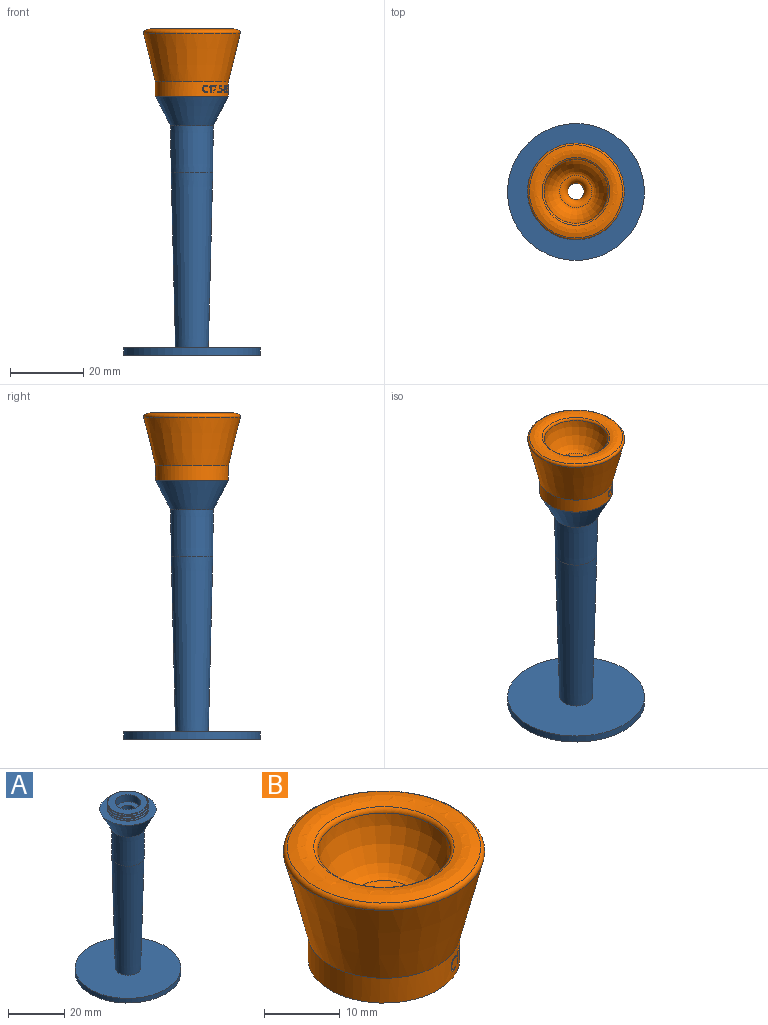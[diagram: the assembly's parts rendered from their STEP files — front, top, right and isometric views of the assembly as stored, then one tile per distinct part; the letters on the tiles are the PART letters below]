
ASSEMBLY  parts=2 mates=1
PART A: 17 faces, bbox 37.8x37.8x74.6 mm
  f0: plane 20.26x20.26mm, normal (0,0,1), area 156.7mm2, adj f4,f12,f13,f14,f15,f16
  f1: plane 37.5x37.5mm, normal (0,0,1), area 1040.8mm2, adj f2,f5
  f2: cone r=4.5mm half-angle=1.4deg, axis (0,0,1), area 1542.8mm2, adj f1,f3
  f3: cone r=5.7mm half-angle=0.6deg, axis (0,0,1), area 463.4mm2, adj f2,f4
  f4: cone r=5.84mm half-angle=27.5deg, axis (0,0,1), area 448.7mm2, adj f0,f3
  f5: cylinder r=18.75mm len=37.5mm, axis (0,0,-1), area 235.6mm2, adj f1,f6
  f6: plane 37.5x37.5mm, normal (0,0,-1), area 1060.3mm2, adj f5,f7
  f7: cylinder r=3.75mm len=7.5mm, axis (0,0,-1), area 47.1mm2, adj f6,f8
  f8: cone r=2.25mm half-angle=1.1deg, axis (0,0,-1), area 1330.3mm2, adj f7,f9
  f9: plane 8.99x8.99mm, normal (0,0,1), area 45.5mm2, adj f8,f10
  f10: cylinder r=4.49mm len=8.99mm, axis (0,0,-1), area 84.7mm2, adj f9,f11
  f11: plane 14.43x14.42mm, normal (0,0,1), area 94mm2, adj f10,f12,f13,f14,f15,f16
  f12: bspline ~15.83x13.71mm, area 36mm2, adj f0,f11,f13,f14
  f13: bspline ~17.08x14.79mm, area 67.9mm2, adj f0,f11,f12,f15
  f14: bspline ~17.08x14.79mm, area 67.9mm2, adj f0,f11,f12,f16
  f15: bspline ~14.81x14.81mm, area 21.6mm2, adj f0,f11,f13,f16
  f16: bspline ~14.81x14.81mm, area 21.6mm2, adj f0,f11,f14,f15
PART B: 291 faces, bbox 28.8x28.8x18.9 mm
  f0: plane 8.39x8.39mm, normal (0,0,-1), area 37.3mm2, adj f6,f285
  f1: cylinder r=10mm len=20mm, axis (0,0,-1), area 236.7mm2, adj f7,f10,f11,f12,f13,f14,f15,f16
  f2: revolved ~25.52x25.52mm, area 248mm2, adj f3,f8
  f3: torus R=9.45mm, axis (0,0,-1), area 50.7mm2, adj f2,f4
  f4: revolved ~17.5x17.5mm, area 429mm2, adj f3,f5
  f5: torus R=4.45mm, axis (0,0,-1), area 65.6mm2, adj f4,f6
  f6: cone r=2.25mm half-angle=1.1deg, axis (0,0,-1), area 107.4mm2, adj f0,f5
  f7: cone r=10mm half-angle=13.8deg, axis (0,0,1), area 997.3mm2, adj f1,f8
  f8: torus R=12.57mm, axis (0,0,-1), area 88.5mm2, adj f2,f7
  f9: cylinder r=9.7mm len=1.96mm, axis (0,0,-1), area 0.9mm2, adj f10,f11,f12,f13,f14,f15,f16,f17
  f10: plane 0.42x0.4mm, normal (0,0,-1), area 0.1mm2, adj f1,f9,f11,f20
  f11: plane 0.25x0.2mm, normal (0.82,-0.57,0), area 0.1mm2, adj f1,f9,f10,f12
  f12: plane 0.42x0.4mm, normal (0,0,1), area 0.1mm2, adj f1,f9,f11,f13
  f13: plane 0.45x0.25mm, normal (0.82,-0.57,0), area 0.1mm2, adj f1,f9,f12,f14
  f14: plane 0.36x0.35mm, normal (0,0,1), area 0.1mm2, adj f1,f9,f13,f15
  f15: plane 0.45x0.25mm, normal (-0.82,0.57,0), area 0.1mm2, adj f1,f9,f14,f16
  f16: plane 0.93x0.81mm, normal (0,0,1), area 0.3mm2, adj f1,f9,f15,f17
  f17: plane 0.25x0.19mm, normal (-0.82,0.57,0), area 0.1mm2, adj f1,f9,f16,f18
  f18: plane 1.32x0.91mm, normal (-0.67,0.46,-0.57), area 0.5mm2, adj f1,f9,f17,f19
  f19: plane 0.38x0.37mm, normal (0,0,-1), area 0.1mm2, adj f1,f9,f18,f20
  f20: plane 1.31x0.25mm, normal (0.82,-0.57,0), area 0.4mm2, adj f1,f9,f10,f19
  f21: extruded ~0.32x0.27mm, area 0.1mm2, adj f9,f22,f26,f279
  f22: plane 0.25x0.18mm, normal (0,0,1), area 0mm2, adj f9,f21,f23,f279
  f23: extruded ~0.43x0.26mm, area 0.1mm2, adj f9,f22,f24,f279
  f24: plane 0.65x0.25mm, normal (-0.82,0.57,0), area 0.2mm2, adj f9,f23,f25,f279
  f25: plane 0.76x0.67mm, normal (0,0,-1), area 0.2mm2, adj f9,f24,f26,f279
  f26: plane 0.86x0.66mm, normal (0.67,-0.46,0.58), area 0.3mm2, adj f9,f21,f25,f279
  f27: cylinder r=9.7mm len=1.97mm, axis (0,0,-1), area 0.8mm2, adj f28,f29,f30,f31,f32,f33,f34,f35
  f28: plane 0.82x0.42mm, normal (0,0,1), area 0.2mm2, adj f1,f27,f29,f46
  f29: plane 0.3x0.2mm, normal (-0.17,-0.99,0), area 0.1mm2, adj f1,f27,f28,f30
  f30: plane 1x0.46mm, normal (0,0,-1), area 0.3mm2, adj f1,f27,f29,f31
  f31: plane 0.91x0.31mm, normal (0.17,0.98,-0.08), area 0.3mm2, adj f1,f27,f30,f32
  f32: plane 0.32x0.16mm, normal (0.09,0.53,0.84), area 0mm2, adj f1,f27,f31,f33
  f33: extruded ~0.39x0.36mm, area 0.1mm2, adj f1,f27,f32,f34
  f34: extruded ~0.54x0.41mm, area 0.2mm2, adj f1,f27,f33,f35
  f35: extruded ~0.32x0.32mm, area 0.1mm2, adj f1,f27,f34,f36
  f36: extruded ~0.41x0.36mm, area 0.1mm2, adj f1,f27,f35,f37
  f37: extruded ~0.35x0.32mm, area 0.1mm2, adj f1,f27,f36,f38
  f38: extruded ~0.35x0.28mm, area 0.1mm2, adj f1,f27,f37,f39
  f39: plane 0.3x0.21mm, normal (0.17,0.99,0), area 0.1mm2, adj f1,f27,f38,f40
  f40: extruded ~0.55x0.4mm, area 0.2mm2, adj f1,f27,f39,f41
  f41: extruded ~0.58x0.39mm, area 0.2mm2, adj f1,f27,f40,f42
  f42: extruded ~0.47x0.34mm, area 0.2mm2, adj f1,f27,f41,f43
  f43: extruded ~0.42x0.34mm, area 0.1mm2, adj f1,f27,f42,f44
  f44: extruded ~0.53x0.39mm, area 0.2mm2, adj f1,f27,f43,f45
  f45: extruded ~0.35x0.35mm, area 0.1mm2, adj f1,f27,f44,f46
  f46: plane 0.58x0.31mm, normal (-0.17,-0.98,0.08), area 0.2mm2, adj f1,f27,f28,f45
  f47: cylinder r=9.7mm len=1.94mm, axis (0,0,-1), area 0.7mm2, adj f48,f49,f50,f51,f52,f53,f54
  f48: plane 0.24x0.19mm, normal (-0.79,-0.62,0), area 0.1mm2, adj f1,f47,f49,f54
  f49: plane 1.21x1.03mm, normal (0,0,-1), area 0.4mm2, adj f1,f47,f48,f50
  f50: plane 0.24x0.2mm, normal (0.79,0.62,0), area 0.1mm2, adj f1,f47,f49,f51
  f51: plane 1.03x0.88mm, normal (0,0,1), area 0.3mm2, adj f1,f47,f50,f52
  f52: plane 1.74x0.82mm, normal (0.71,0.56,-0.42), area 0.6mm2, adj f1,f47,f51,f53
  f53: plane 0.38x0.38mm, normal (0,0,1), area 0.1mm2, adj f1,f47,f52,f54
  f54: plane 1.77x0.8mm, normal (-0.72,-0.56,0.41), area 0.6mm2, adj f1,f47,f48,f53
  f55: cylinder r=9.7mm len=1.94mm, axis (0,0,-1), area 0.5mm2, adj f56,f57,f58,f59,f60,f61,f62,f63
  f56: plane 0.6x0.52mm, normal (0.53,0.31,-0.79), area 0.2mm2, adj f1,f55,f57,f64
  f57: plane 0.32x0.25mm, normal (0.68,0.4,0.61), area 0.1mm2, adj f1,f55,f56,f58
  f58: extruded ~0.43x0.42mm, area 0.1mm2, adj f1,f55,f57,f59
  f59: extruded ~0.29x0.21mm, area 0mm2, adj f1,f55,f58,f60
  f60: extruded ~0.33x0.27mm, area 0.1mm2, adj f1,f55,f59,f61
  f61: plane 1.39x0.26mm, normal (0.86,0.5,0), area 0.4mm2, adj f1,f55,f60,f62
  f62: plane 0.37x0.33mm, normal (0,0,1), area 0.1mm2, adj f1,f55,f61,f63
  f63: plane 1.94x0.26mm, normal (-0.86,-0.5,0), area 0.6mm2, adj f1,f55,f62,f64
  f64: plane 0.36x0.31mm, normal (0,0,-1), area 0.1mm2, adj f1,f55,f56,f63
  f65: cylinder r=9.7mm len=1.97mm, axis (0,0,-1), area 0.8mm2, adj f66,f67,f68,f69,f70,f71,f72,f73
  f66: plane 0.8x0.71mm, normal (0,0,1), area 0.2mm2, adj f1,f65,f67,f84
  f67: plane 0.24x0.2mm, normal (-0.62,-0.78,0), area 0.1mm2, adj f1,f65,f66,f68
  f68: plane 0.94x0.84mm, normal (0,0,-1), area 0.3mm2, adj f1,f65,f67,f69
  f69: plane 0.91x0.28mm, normal (0.62,0.78,-0.08), area 0.3mm2, adj f1,f65,f68,f70
  f70: plane 0.31x0.27mm, normal (0.33,0.42,0.84), area 0mm2, adj f1,f65,f69,f71
  f71: extruded ~0.46x0.45mm, area 0.1mm2, adj f1,f65,f70,f72
  f72: extruded ~0.58x0.55mm, area 0.2mm2, adj f1,f65,f71,f73
  f73: extruded ~0.32x0.32mm, area 0.1mm2, adj f1,f65,f72,f74
  f74: extruded ~0.47x0.46mm, area 0.1mm2, adj f1,f65,f73,f75
  f75: extruded ~0.41x0.4mm, area 0.1mm2, adj f1,f65,f74,f76
  f76: extruded ~0.39x0.37mm, area 0.1mm2, adj f1,f65,f75,f77
  f77: plane 0.24x0.21mm, normal (0.62,0.78,0), area 0.1mm2, adj f1,f65,f76,f78
  f78: extruded ~0.59x0.56mm, area 0.2mm2, adj f1,f65,f77,f79
  f79: extruded ~0.61x0.57mm, area 0.2mm2, adj f1,f65,f78,f80
  f80: extruded ~0.47x0.36mm, area 0.2mm2, adj f1,f65,f79,f81
  f81: extruded ~0.42x0.35mm, area 0.1mm2, adj f1,f65,f80,f82
  f82: extruded ~0.57x0.54mm, area 0.2mm2, adj f1,f65,f81,f83
  f83: extruded ~0.43x0.43mm, area 0.1mm2, adj f1,f65,f82,f84
  f84: plane 0.58x0.27mm, normal (-0.62,-0.78,0.08), area 0.2mm2, adj f1,f65,f66,f83
  f85: cylinder r=9.7mm len=2mm, axis (0,0,-1), area 0.8mm2, adj f86,f87,f88,f89,f90,f91,f92,f93
  f86: extruded ~0.62x0.5mm, area 0.2mm2, adj f1,f85,f87,f100
  f87: extruded ~0.58x0.46mm, area 0.2mm2, adj f1,f85,f86,f88
  f88: extruded ~0.42x0.41mm, area 0.1mm2, adj f1,f85,f87,f89
  f89: extruded ~0.53x0.33mm, area 0.2mm2, adj f1,f85,f88,f90
  f90: extruded ~0.74x0.38mm, area 0.2mm2, adj f1,f85,f89,f91
  f91: extruded ~0.73x0.53mm, area 0.2mm2, adj f1,f85,f90,f92
  f92: extruded ~0.58x0.48mm, area 0.2mm2, adj f1,f85,f91,f93
  f93: plane 0.28x0.2mm, normal (-0.93,-0.37,0), area 0.1mm2, adj f1,f85,f92,f94
  f94: extruded ~0.55x0.47mm, area 0.1mm2, adj f1,f85,f93,f95
  f95: extruded ~0.59x0.47mm, area 0.2mm2, adj f1,f85,f94,f96
  f96: extruded ~0.59x0.35mm, area 0.2mm2, adj f1,f85,f95,f97
  f97: extruded ~0.58x0.35mm, area 0.2mm2, adj f1,f85,f96,f98
  f98: extruded ~0.58x0.47mm, area 0.2mm2, adj f1,f85,f97,f99
  f99: extruded ~0.53x0.46mm, area 0.1mm2, adj f1,f85,f98,f100
  f100: plane 0.32x0.2mm, normal (-0.83,-0.33,0.44), area 0.1mm2, adj f1,f85,f86,f99
  f101: cylinder r=9.7mm len=2mm, axis (0,0,-1), area 1mm2, adj f102,f103,f104,f105,f106,f107,f108,f109
  f102: extruded ~0.35x0.34mm, area 0.1mm2, adj f1,f101,f103,f116
  f103: extruded ~0.51x0.45mm, area 0.1mm2, adj f1,f101,f102,f104
  f104: extruded ~0.51x0.45mm, area 0.1mm2, adj f1,f101,f103,f105
  f105: extruded ~0.34x0.34mm, area 0.1mm2, adj f1,f101,f104,f106
  f106: extruded ~0.32x0.26mm, area 0.1mm2, adj f1,f101,f105,f107
  f107: extruded ~0.4x0.38mm, area 0.1mm2, adj f1,f101,f106,f108
  f108: extruded ~0.43x0.42mm, area 0.1mm2, adj f1,f101,f107,f109
  f109: extruded ~0.32x0.29mm, area 0.1mm2, adj f1,f101,f108,f110
  f110: extruded ~0.39x0.35mm, area 0.1mm2, adj f1,f101,f109,f111
  f111: extruded ~0.55x0.47mm, area 0.1mm2, adj f1,f101,f110,f112
  f112: extruded ~0.56x0.48mm, area 0.2mm2, adj f1,f101,f111,f113
  f113: extruded ~0.39x0.35mm, area 0.1mm2, adj f1,f101,f112,f114
  f114: extruded ~0.52x0.5mm, area 0.2mm2, adj f1,f101,f113,f115
  f115: extruded ~0.39x0.37mm, area 0.1mm2, adj f1,f101,f114,f116
  f116: extruded ~0.31x0.27mm, area 0.1mm2, adj f1,f101,f102,f115
  f117: extruded ~0.4x0.39mm, area 0.1mm2, adj f101,f118,f124,f133
  f118: extruded ~0.31x0.25mm, area 0.1mm2, adj f101,f117,f119,f133
  f119: extruded ~0.32x0.25mm, area 0.1mm2, adj f101,f118,f120,f133
  f120: extruded ~0.41x0.4mm, area 0.1mm2, adj f101,f119,f121,f133
  f121: extruded ~0.4x0.4mm, area 0.1mm2, adj f101,f120,f122,f133
  f122: extruded ~0.32x0.26mm, area 0.1mm2, adj f101,f121,f123,f133
  f123: extruded ~0.32x0.23mm, area 0.1mm2, adj f101,f122,f124,f133
  f124: extruded ~0.45x0.42mm, area 0.1mm2, adj f101,f117,f123,f133
  f125: extruded ~0.31x0.21mm, area 0.1mm2, adj f101,f126,f132,f280
  f126: extruded ~0.39x0.37mm, area 0.1mm2, adj f101,f125,f127,f280
  f127: extruded ~0.39x0.39mm, area 0.1mm2, adj f101,f126,f128,f280
  f128: extruded ~0.31x0.21mm, area 0.1mm2, adj f101,f127,f129,f280
  f129: extruded ~0.32x0.21mm, area 0.1mm2, adj f101,f128,f130,f280
  f130: extruded ~0.38x0.36mm, area 0.1mm2, adj f101,f129,f131,f280
  f131: extruded ~0.38x0.36mm, area 0.1mm2, adj f101,f130,f132,f280
  f132: extruded ~0.32x0.21mm, area 0.1mm2, adj f101,f125,f131,f280
  f133: cylinder r=10mm len=0.77mm, axis (0,0,-1), area 0.5mm2, adj f117,f118,f119,f120,f121,f122,f123,f124
  f134: cylinder r=9.7mm len=0.56mm, axis (0,0,-1), area 0.1mm2, adj f135,f136,f137,f138
  f135: plane 0.71x0.59mm, normal (0,0,-1), area 0.2mm2, adj f1,f134,f136,f138
  f136: plane 0.26x0.2mm, normal (0.51,0.86,0), area 0.1mm2, adj f1,f134,f135,f137
  f137: plane 0.71x0.59mm, normal (0,0,1), area 0.2mm2, adj f1,f134,f136,f138
  f138: plane 0.26x0.2mm, normal (-0.51,-0.86,0), area 0.1mm2, adj f1,f134,f135,f137
  f139: cylinder r=9.7mm len=0.36mm, axis (0,0,-1), area 0.1mm2, adj f140,f141,f142,f143,f144,f145,f146,f147
  f140: extruded ~0.32x0.2mm, area 0mm2, adj f1,f139,f141,f147
  f141: extruded ~0.3x0.13mm, area 0mm2, adj f1,f139,f140,f142
  f142: extruded ~0.3x0.14mm, area 0mm2, adj f1,f139,f141,f143
  f143: extruded ~0.32x0.2mm, area 0mm2, adj f1,f139,f142,f144
  f144: extruded ~0.32x0.2mm, area 0mm2, adj f1,f139,f143,f145
  f145: extruded ~0.3x0.14mm, area 0mm2, adj f1,f139,f144,f146
  f146: extruded ~0.3x0.14mm, area 0mm2, adj f1,f139,f145,f147
  f147: extruded ~0.32x0.19mm, area 0mm2, adj f1,f139,f140,f146
  f148: cylinder r=9.7mm len=1.94mm, axis (0,0,-1), area 1.1mm2, adj f149,f150,f151,f152,f153,f154,f155,f156
  f149: plane 0.81x0.5mm, normal (-0.09,0.86,0.5), area 0.3mm2, adj f1,f148,f150,f159
  f150: plane 0.44x0.33mm, normal (0,0,1), area 0.1mm2, adj f1,f148,f149,f151
  f151: plane 0.81x0.3mm, normal (0.1,-1,0), area 0.2mm2, adj f1,f148,f150,f152
  f152: plane 0.31x0.26mm, normal (0,0,1), area 0.1mm2, adj f1,f148,f151,f153
  f153: plane 1.94x0.3mm, normal (-0.1,1,0), area 0.6mm2, adj f1,f148,f152,f154
  f154: plane 0.56x0.33mm, normal (0,0,-1), area 0.2mm2, adj f1,f148,f153,f155
  f155: extruded ~0.56x0.36mm, area 0.2mm2, adj f1,f148,f154,f156
  f156: extruded ~0.41x0.32mm, area 0.1mm2, adj f1,f148,f155,f157
  f157: extruded ~0.52x0.42mm, area 0.2mm2, adj f1,f148,f156,f158
  f158: plane 0.87x0.55mm, normal (0.09,-0.85,-0.52), area 0.3mm2, adj f1,f148,f157,f159
  f159: plane 0.34x0.29mm, normal (0,0,1), area 0.1mm2, adj f1,f148,f149,f158
  f160: extruded ~0.39x0.34mm, area 0.1mm2, adj f148,f161,f166,f281
  f161: extruded ~0.31x0.28mm, area 0.1mm2, adj f148,f160,f162,f281
  f162: extruded ~0.31x0.29mm, area 0.1mm2, adj f148,f161,f163,f281
  f163: extruded ~0.38x0.34mm, area 0.1mm2, adj f148,f162,f164,f281
  f164: plane 0.34x0.32mm, normal (0,0,-1), area 0.1mm2, adj f148,f163,f165,f281
  f165: plane 0.74x0.3mm, normal (0.1,-1,0), area 0.2mm2, adj f148,f164,f166,f281
  f166: plane 0.32x0.32mm, normal (0,0,1), area 0.1mm2, adj f148,f160,f165,f281
  f167: cylinder r=9.7mm len=0.36mm, axis (0,0,-1), area 0.1mm2, adj f168,f169,f170,f171,f172,f173,f174,f175
  f168: extruded ~0.32x0.25mm, area 0mm2, adj f1,f167,f169,f175
  f169: extruded ~0.29x0.18mm, area 0mm2, adj f1,f167,f168,f170
  f170: extruded ~0.29x0.18mm, area 0mm2, adj f1,f167,f169,f171
  f171: extruded ~0.32x0.25mm, area 0mm2, adj f1,f167,f170,f172
  f172: extruded ~0.32x0.24mm, area 0mm2, adj f1,f167,f171,f173
  f173: extruded ~0.29x0.18mm, area 0mm2, adj f1,f167,f172,f174
  f174: extruded ~0.29x0.18mm, area 0mm2, adj f1,f167,f173,f175
  f175: extruded ~0.32x0.24mm, area 0mm2, adj f1,f167,f168,f174
  f176: cylinder r=9.7mm len=1.97mm, axis (0,0,-1), area 0.8mm2, adj f177,f178,f179,f180,f181,f182,f183,f184
  f177: plane 0.84x0.55mm, normal (0,0,1), area 0.2mm2, adj f1,f176,f178,f195
  f178: plane 0.28x0.2mm, normal (0.93,-0.36,0), area 0.1mm2, adj f1,f176,f177,f179
  f179: plane 1.01x0.63mm, normal (0,0,-1), area 0.3mm2, adj f1,f176,f178,f180
  f180: plane 0.91x0.31mm, normal (-0.93,0.35,-0.08), area 0.3mm2, adj f1,f176,f179,f181
  f181: plane 0.33x0.21mm, normal (-0.5,0.19,0.84), area 0mm2, adj f1,f176,f180,f182
  f182: extruded ~0.43x0.41mm, area 0.1mm2, adj f1,f176,f181,f183
  f183: extruded ~0.58x0.46mm, area 0.2mm2, adj f1,f176,f182,f184
  f184: extruded ~0.33x0.32mm, area 0.1mm2, adj f1,f176,f183,f185
  f185: extruded ~0.45x0.41mm, area 0.1mm2, adj f1,f176,f184,f186
  f186: extruded ~0.38x0.36mm, area 0.1mm2, adj f1,f176,f185,f187
  f187: extruded ~0.37x0.33mm, area 0.1mm2, adj f1,f176,f186,f188
  f188: plane 0.28x0.21mm, normal (-0.93,0.36,0), area 0.1mm2, adj f1,f176,f187,f189
  f189: extruded ~0.58x0.48mm, area 0.2mm2, adj f1,f176,f188,f190
  f190: extruded ~0.61x0.48mm, area 0.2mm2, adj f1,f176,f189,f191
  f191: extruded ~0.47x0.36mm, area 0.2mm2, adj f1,f176,f190,f192
  f192: extruded ~0.42x0.35mm, area 0.1mm2, adj f1,f176,f191,f193
  f193: extruded ~0.56x0.46mm, area 0.2mm2, adj f1,f176,f192,f194
  f194: extruded ~0.39x0.39mm, area 0.1mm2, adj f1,f176,f193,f195
  f195: plane 0.58x0.3mm, normal (0.93,-0.35,0.08), area 0.2mm2, adj f1,f176,f177,f194
  f196: cylinder r=9.7mm len=1.94mm, axis (0,0,-1), area 1.3mm2, adj f197,f198,f199,f200,f201,f202,f203,f204
  f197: plane 0.71x0.68mm, normal (0,0,1), area 0.2mm2, adj f1,f196,f198,f207
  f198: plane 1.94x0.21mm, normal (-0.71,0.7,0), area 0.6mm2, adj f1,f196,f197,f199
  f199: plane 0.61x0.59mm, normal (0,0,-1), area 0.2mm2, adj f1,f196,f198,f200
  f200: extruded ~0.62x0.62mm, area 0.2mm2, adj f1,f196,f199,f201
  f201: extruded ~0.37x0.34mm, area 0.1mm2, adj f1,f196,f200,f202
  f202: extruded ~0.29x0.29mm, area 0.1mm2, adj f1,f196,f201,f203
  f203: extruded ~0.42x0.42mm, area 0.1mm2, adj f1,f196,f202,f204
  f204: plane 0.21x0.21mm, normal (0.71,-0.7,0), area 0mm2, adj f1,f196,f203,f205
  f205: extruded ~0.54x0.54mm, area 0.2mm2, adj f1,f196,f204,f206
  f206: extruded ~0.41x0.35mm, area 0.1mm2, adj f1,f196,f205,f207
  f207: extruded ~0.57x0.57mm, area 0.2mm2, adj f1,f196,f197,f206
  f208: plane 0.45x0.44mm, normal (0,0,1), area 0.1mm2, adj f196,f209,f214,f222
  f209: plane 0.64x0.21mm, normal (0.71,-0.7,0), area 0.2mm2, adj f196,f208,f210,f222
  f210: plane 0.48x0.47mm, normal (0,0,-1), area 0.1mm2, adj f196,f209,f211,f222
  f211: extruded ~0.46x0.46mm, area 0.1mm2, adj f196,f210,f212,f222
  f212: extruded ~0.29x0.29mm, area 0.1mm2, adj f196,f211,f213,f222
  f213: extruded ~0.3x0.3mm, area 0.1mm2, adj f196,f212,f214,f222
  f214: extruded ~0.48x0.48mm, area 0.1mm2, adj f196,f208,f213,f222
  f215: extruded ~0.3x0.3mm, area 0.1mm2, adj f196,f216,f221,f282
  f216: extruded ~0.3x0.3mm, area 0.1mm2, adj f196,f215,f217,f282
  f217: extruded ~0.47x0.47mm, area 0.1mm2, adj f196,f216,f218,f282
  f218: plane 0.51x0.49mm, normal (0,0,-1), area 0.1mm2, adj f196,f217,f219,f282
  f219: plane 0.73x0.21mm, normal (0.71,-0.7,0), area 0.2mm2, adj f196,f218,f220,f282
  f220: plane 0.49x0.48mm, normal (0,0,1), area 0.1mm2, adj f196,f219,f221,f282
  f221: extruded ~0.48x0.48mm, area 0.1mm2, adj f196,f215,f220,f282
  f222: cylinder r=10mm len=0.64mm, axis (0,0,-1), area 0.5mm2, adj f208,f209,f210,f211,f212,f213,f214
  f223: cylinder r=9.7mm len=0.36mm, axis (0,0,-1), area 0.1mm2, adj f224,f225,f226,f227,f228,f229,f230,f231
  f224: extruded ~0.3x0.3mm, area 0mm2, adj f1,f223,f225,f231
  f225: extruded ~0.24x0.24mm, area 0mm2, adj f1,f223,f224,f226
  f226: extruded ~0.24x0.24mm, area 0mm2, adj f1,f223,f225,f227
  f227: extruded ~0.3x0.3mm, area 0mm2, adj f1,f223,f226,f228
  f228: extruded ~0.3x0.29mm, area 0mm2, adj f1,f223,f227,f229
  f229: extruded ~0.24x0.24mm, area 0mm2, adj f1,f223,f228,f230
  f230: extruded ~0.24x0.24mm, area 0mm2, adj f1,f223,f229,f231
  f231: extruded ~0.29x0.29mm, area 0mm2, adj f1,f223,f224,f230
  f232: cylinder r=9.7mm len=0.36mm, axis (0,0,-1), area 0.1mm2, adj f233,f234,f235,f236,f237,f238,f239,f240
  f233: extruded ~0.32x0.23mm, area 0mm2, adj f1,f232,f234,f240
  f234: extruded ~0.29x0.16mm, area 0mm2, adj f1,f232,f233,f235
  f235: extruded ~0.29x0.16mm, area 0mm2, adj f1,f232,f234,f236
  f236: extruded ~0.32x0.23mm, area 0mm2, adj f1,f232,f235,f237
  f237: extruded ~0.32x0.22mm, area 0mm2, adj f1,f232,f236,f238
  f238: extruded ~0.29x0.16mm, area 0mm2, adj f1,f232,f237,f239
  f239: extruded ~0.29x0.16mm, area 0mm2, adj f1,f232,f238,f240
  f240: extruded ~0.32x0.22mm, area 0mm2, adj f1,f232,f233,f239
  f241: cylinder r=9.7mm len=1.97mm, axis (0,0,-1), area 0.8mm2, adj f242,f243,f244,f245,f246,f247,f248,f249
  f242: plane 0.82x0.65mm, normal (0,0,1), area 0.2mm2, adj f1,f241,f243,f260
  f243: plane 0.26x0.2mm, normal (0.5,-0.87,0), area 0.1mm2, adj f1,f241,f242,f244
  f244: plane 0.99x0.74mm, normal (0,0,-1), area 0.3mm2, adj f1,f241,f243,f245
  f245: plane 0.91x0.29mm, normal (-0.49,0.87,-0.08), area 0.3mm2, adj f1,f241,f244,f246
  f246: plane 0.31x0.25mm, normal (-0.27,0.47,0.84), area 0mm2, adj f1,f241,f245,f247
  f247: extruded ~0.45x0.44mm, area 0.1mm2, adj f1,f241,f246,f248
  f248: extruded ~0.59x0.51mm, area 0.2mm2, adj f1,f241,f247,f249
  f249: extruded ~0.33x0.32mm, area 0.1mm2, adj f1,f241,f248,f250
  f250: extruded ~0.47x0.44mm, area 0.1mm2, adj f1,f241,f249,f251
  f251: extruded ~0.4x0.39mm, area 0.1mm2, adj f1,f241,f250,f252
  f252: extruded ~0.39x0.36mm, area 0.1mm2, adj f1,f241,f251,f253
  f253: plane 0.26x0.21mm, normal (-0.5,0.87,0), area 0.1mm2, adj f1,f241,f252,f254
  f254: extruded ~0.59x0.53mm, area 0.2mm2, adj f1,f241,f253,f255
  f255: extruded ~0.61x0.53mm, area 0.2mm2, adj f1,f241,f254,f256
  f256: extruded ~0.47x0.37mm, area 0.2mm2, adj f1,f241,f255,f257
  f257: extruded ~0.42x0.36mm, area 0.1mm2, adj f1,f241,f256,f258
  f258: extruded ~0.57x0.51mm, area 0.2mm2, adj f1,f241,f257,f259
  f259: extruded ~0.42x0.42mm, area 0.1mm2, adj f1,f241,f258,f260
  f260: plane 0.58x0.28mm, normal (0.49,-0.87,0.08), area 0.2mm2, adj f1,f241,f242,f259
  f261: cylinder r=9.7mm len=1.96mm, axis (0,0,-1), area 0.9mm2, adj f262,f263,f264,f265,f266,f267,f268,f269
  f262: plane 0.38x0.36mm, normal (0,0,-1), area 0.1mm2, adj f1,f261,f263,f272
  f263: plane 0.29x0.2mm, normal (0.27,-0.96,0), area 0.1mm2, adj f1,f261,f262,f264
  f264: plane 0.38x0.36mm, normal (0,0,1), area 0.1mm2, adj f1,f261,f263,f265
  f265: plane 0.45x0.29mm, normal (0.27,-0.96,0), area 0.1mm2, adj f1,f261,f264,f266
  f266: plane 0.35x0.28mm, normal (0,0,1), area 0.1mm2, adj f1,f261,f265,f267
  f267: plane 0.45x0.29mm, normal (-0.27,0.96,0), area 0.1mm2, adj f1,f261,f266,f268
  f268: plane 1x0.52mm, normal (0,0,1), area 0.3mm2, adj f1,f261,f267,f269
  f269: plane 0.29x0.19mm, normal (-0.27,0.96,0), area 0.1mm2, adj f1,f261,f268,f270
  f270: plane 1.32x0.98mm, normal (-0.23,0.79,-0.57), area 0.5mm2, adj f1,f261,f269,f271
  f271: plane 0.36x0.31mm, normal (0,0,-1), area 0.1mm2, adj f1,f261,f270,f272
  f272: plane 1.31x0.29mm, normal (0.27,-0.96,0), area 0.4mm2, adj f1,f261,f262,f271
  f273: extruded ~0.32x0.21mm, area 0.1mm2, adj f261,f274,f278,f283
  f274: plane 0.29x0.09mm, normal (0,0,1), area 0mm2, adj f261,f273,f275,f283
  f275: extruded ~0.43x0.29mm, area 0.1mm2, adj f261,f274,f276,f283
  f276: plane 0.65x0.29mm, normal (-0.27,0.96,0), area 0.2mm2, adj f261,f275,f277,f283
  f277: plane 0.78x0.47mm, normal (0,0,-1), area 0.2mm2, adj f261,f276,f278,f283
  f278: plane 0.86x0.67mm, normal (0.22,-0.79,0.58), area 0.3mm2, adj f261,f273,f277,f283
  f279: cylinder r=10mm len=1.08mm, axis (0,0,-1), area 0.4mm2, adj f21,f22,f23,f24,f25,f26
  f280: cylinder r=10mm len=0.68mm, axis (0,0,-1), area 0.3mm2, adj f125,f126,f127,f128,f129,f130,f131,f132
  f281: cylinder r=10mm len=0.77mm, axis (0,0,-1), area 0.5mm2, adj f160,f161,f162,f163,f164,f165,f166
  f282: cylinder r=10mm len=0.73mm, axis (0,0,-1), area 0.6mm2, adj f215,f216,f217,f218,f219,f220,f221
  f283: cylinder r=10mm len=1.08mm, axis (0,0,-1), area 0.4mm2, adj f273,f274,f275,f276,f277,f278
  f284: plane 20.06x20.06mm, normal (0,0,-1), area 140.3mm2, adj f1,f286,f288,f289,f290
  f285: cylinder r=4.19mm len=8.39mm, axis (0,0,-1), area 84.3mm2, adj f0,f287
  f286: cylinder r=7.59mm len=15.19mm, axis (0,0,-1), area 18.9mm2, adj f284,f287,f288,f289
  f287: plane 15.02x14.89mm, normal (0,0,-1), area 118.6mm2, adj f285,f286,f288,f289,f290
  f288: bspline ~15.21x15.21mm, area 31.9mm2, adj f284,f286,f287
  f289: bspline ~15.21x15.21mm, area 31.9mm2, adj f284,f286,f287
  f290: bspline ~14.7x14.7mm, area 61.2mm2, adj f284,f287
PLACE A rot(axis=(0,0,1),24.8deg) t=(5.59,-8.82,3.52)mm
PLACE B t=(5.59,-8.82,3.59)mm
MATE cylindrical B.f1 <-> A.f2  axis (0,0,-1) through (5.59,-8.82,72.49)mm
